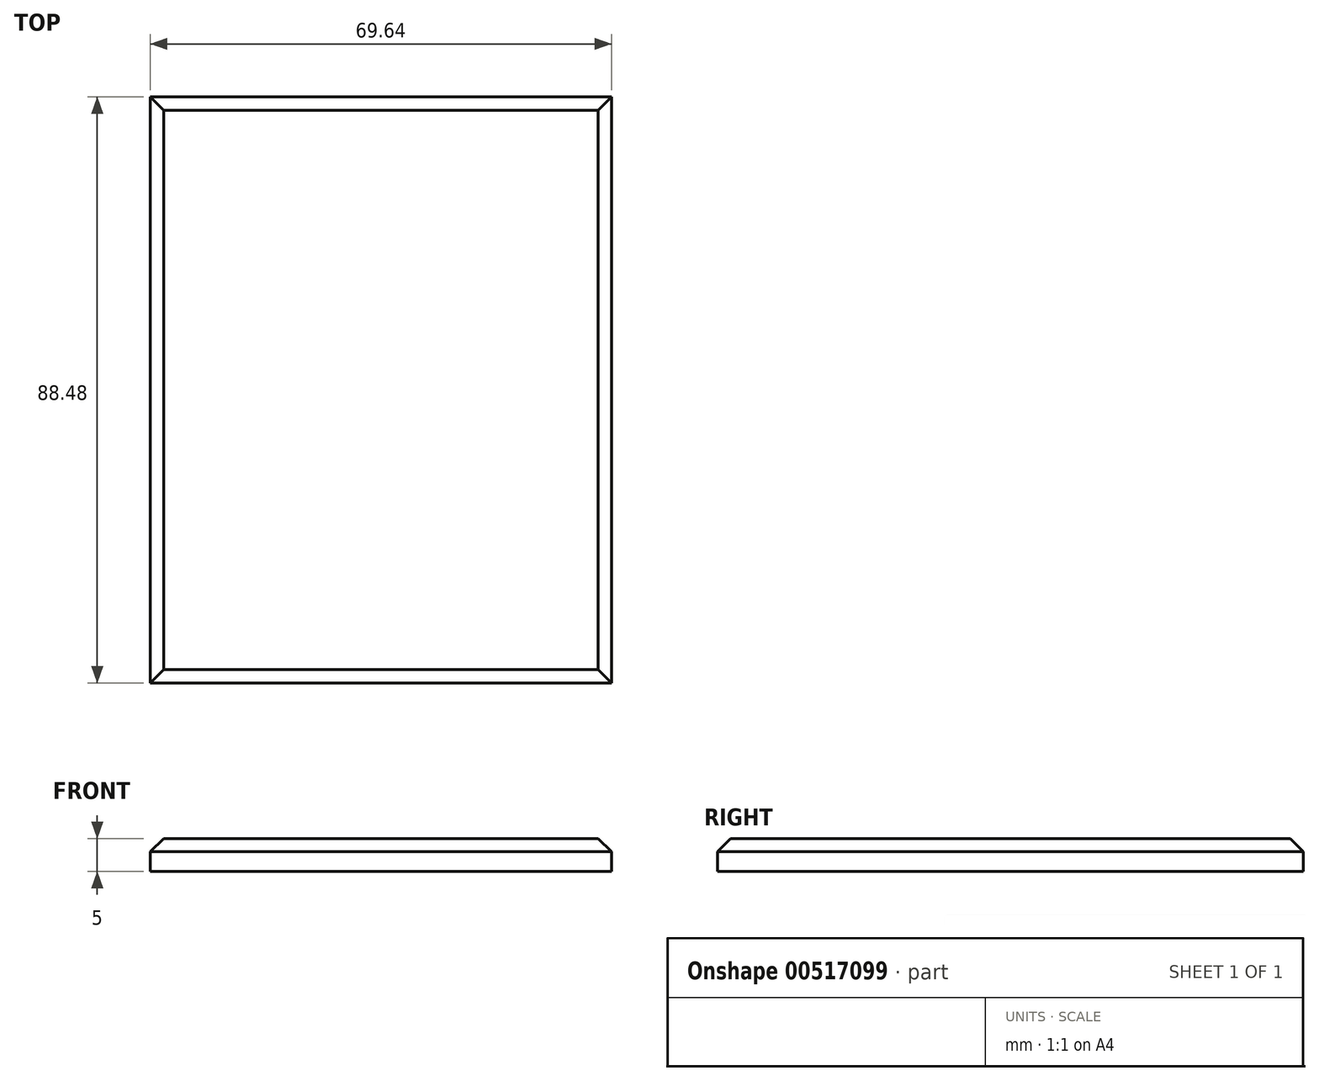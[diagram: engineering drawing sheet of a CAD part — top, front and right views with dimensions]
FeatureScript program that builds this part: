
annotation { "Feature Type Name" : "Feature", "Feature Type Description" : "" }
export const myFeature = defineFeature(function(context is Context, id is Id, definition is map)
    precondition{}
    {
        {
            var Q0;
            Q0=qCreatedBy(makeId("Top.planeOp"),FACE);
            var sketch = newSketch(context, id + "F0", { "sketchPlane" : qUnion([Q0])});
            skLineSegment(sketch, "E0.bottom", {"start": v(-92.74, -46.83) * mm, "end": v(-23.1, -46.83) * mm});
            skLineSegment(sketch, "E0.top", {"start": v(-92.74, 41.65) * mm, "end": v(-23.1, 41.65) * mm});
            skLineSegment(sketch, "E0.left", {"start": v(-92.74, -46.83) * mm, "end": v(-92.74, 41.65) * mm});
            skLineSegment(sketch, "E0.right", {"start": v(-23.1, -46.83) * mm, "end": v(-23.1, 41.65) * mm});
            skSolve(sketch);
        }
        {
            var Q0;
            Q0 = qSketchRegion(id + "F0", true);
            extrude(context, id + "F1", {"entities" : qUnion([Q0]), "depth" : 5 * mm, "offsetDistance" : 25 * mm});
        }
        {
            var Q0;
            Q0=makeQuery(id+"F1.opExtrude","CAP_EDGE",EDGE,{"disambiguationData":[OSD([sQuery(id+"F0.wireOp",EDGE,"E0.bottom")])],"isStart":false});
            var Q1;
            Q1=makeQuery(id+"F1.opExtrude","CAP_EDGE",EDGE,{"disambiguationData":[OSD([sQuery(id+"F0.wireOp",EDGE,"E0.left")])],"isStart":false});
            var Q2;
            Q2=makeQuery(id+"F1.opExtrude","CAP_EDGE",EDGE,{"disambiguationData":[OSD([sQuery(id+"F0.wireOp",EDGE,"E0.right")])],"isStart":false});
            var Q3;
            Q3=makeQuery(id+"F1.opExtrude","CAP_EDGE",EDGE,{"disambiguationData":[OSD([sQuery(id+"F0.wireOp",EDGE,"E0.top")])],"isStart":false});
            chamfer(context, id + "F2", {"entities" : qUnion([Q0, Q1, Q2, Q3]), "width" : 2 * mm, "tangentPropagation" : true});
        }
    });
